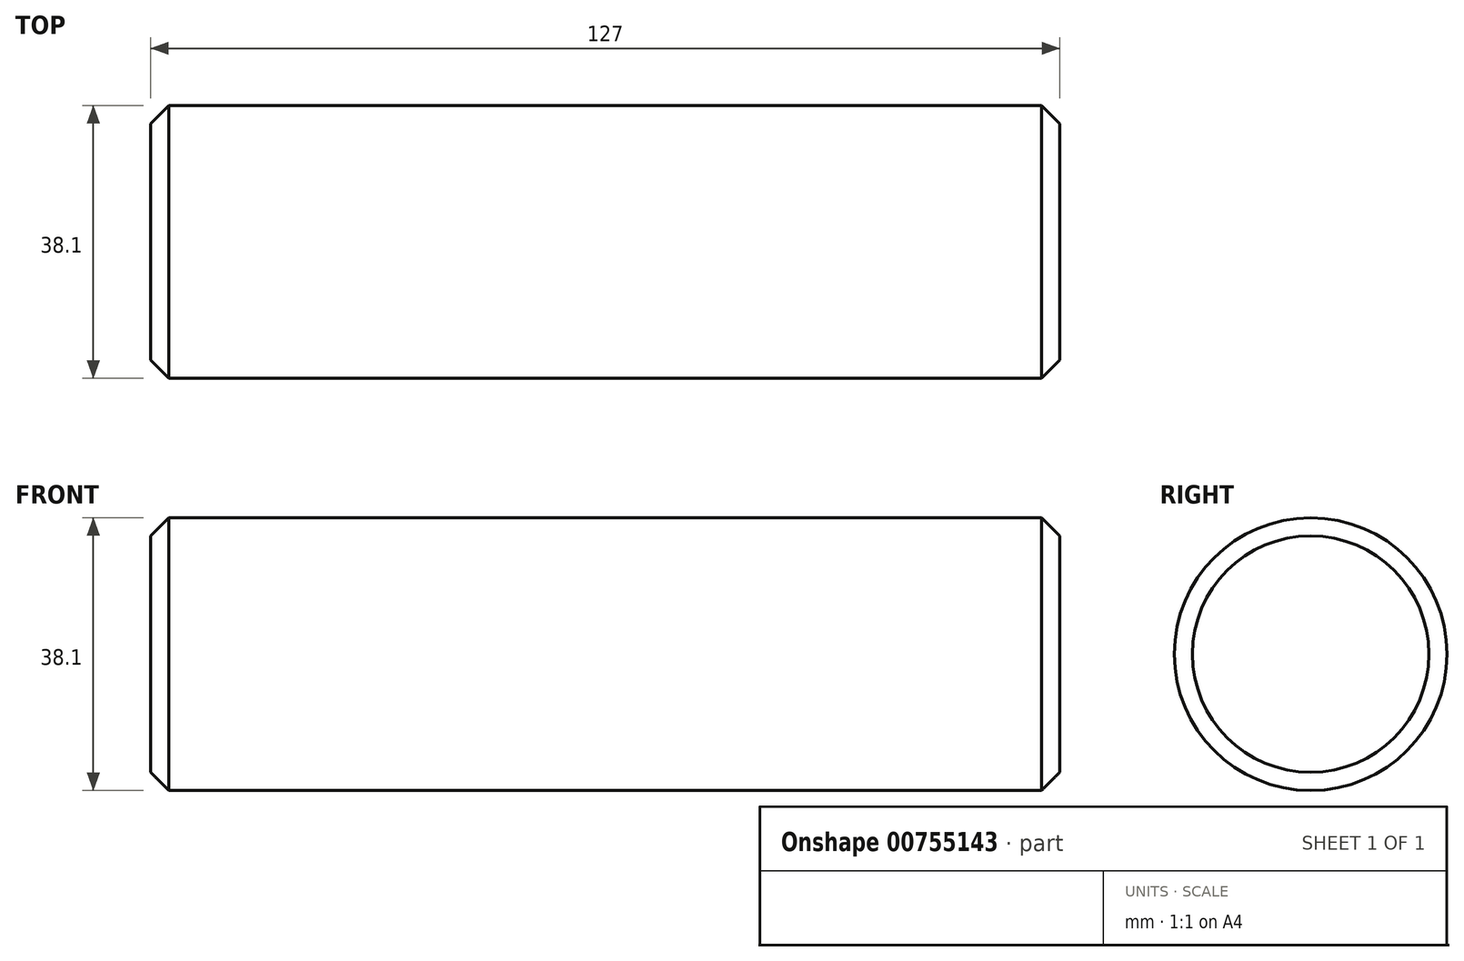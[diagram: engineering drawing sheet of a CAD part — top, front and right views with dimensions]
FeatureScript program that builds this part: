
annotation { "Feature Type Name" : "Feature", "Feature Type Description" : "" }
export const myFeature = defineFeature(function(context is Context, id is Id, definition is map)
    precondition{}
    {
        {
            var Q0;
            Q0=qCreatedBy(makeId("Right.planeOp"),FACE);
            var sketch = newSketch(context, id + "F0", { "sketchPlane" : qUnion([Q0])});
            skCircle(sketch, "E0", {"center": v(0, 0) * mm, "radius": 19.05 * mm});
            skSolve(sketch);
        }
        {
            var Q0;
            Q0 = qSketchRegion(id + "F0", true);
            extrude(context, id + "F1", {"entities" : qUnion([Q0]), "depth" : 63.5 * mm, "offsetDistance" : 25.4 * mm, "hasSecondDirection" : true, "secondDirectionOppositeDirection" : true, "secondDirectionDepth" : 63.5 * mm});
        }
        {
            var Q0;
            Q0=makeQuery(id+"F1.opExtrude","CAP_EDGE",EDGE,{"disambiguationData":[OSD([sQuery(id+"F0.wireOp",EDGE,"E0")])],"isStart":true});
            var Q1;
            Q1=makeQuery(id+"F1.opExtrude","CAP_EDGE",EDGE,{"disambiguationData":[OSD([sQuery(id+"F0.wireOp",EDGE,"E0")])],"isStart":false});
            chamfer(context, id + "F2", {"entities" : qUnion([Q0, Q1]), "width" : 2.54 * mm, "tangentPropagation" : true});
        }
    });
